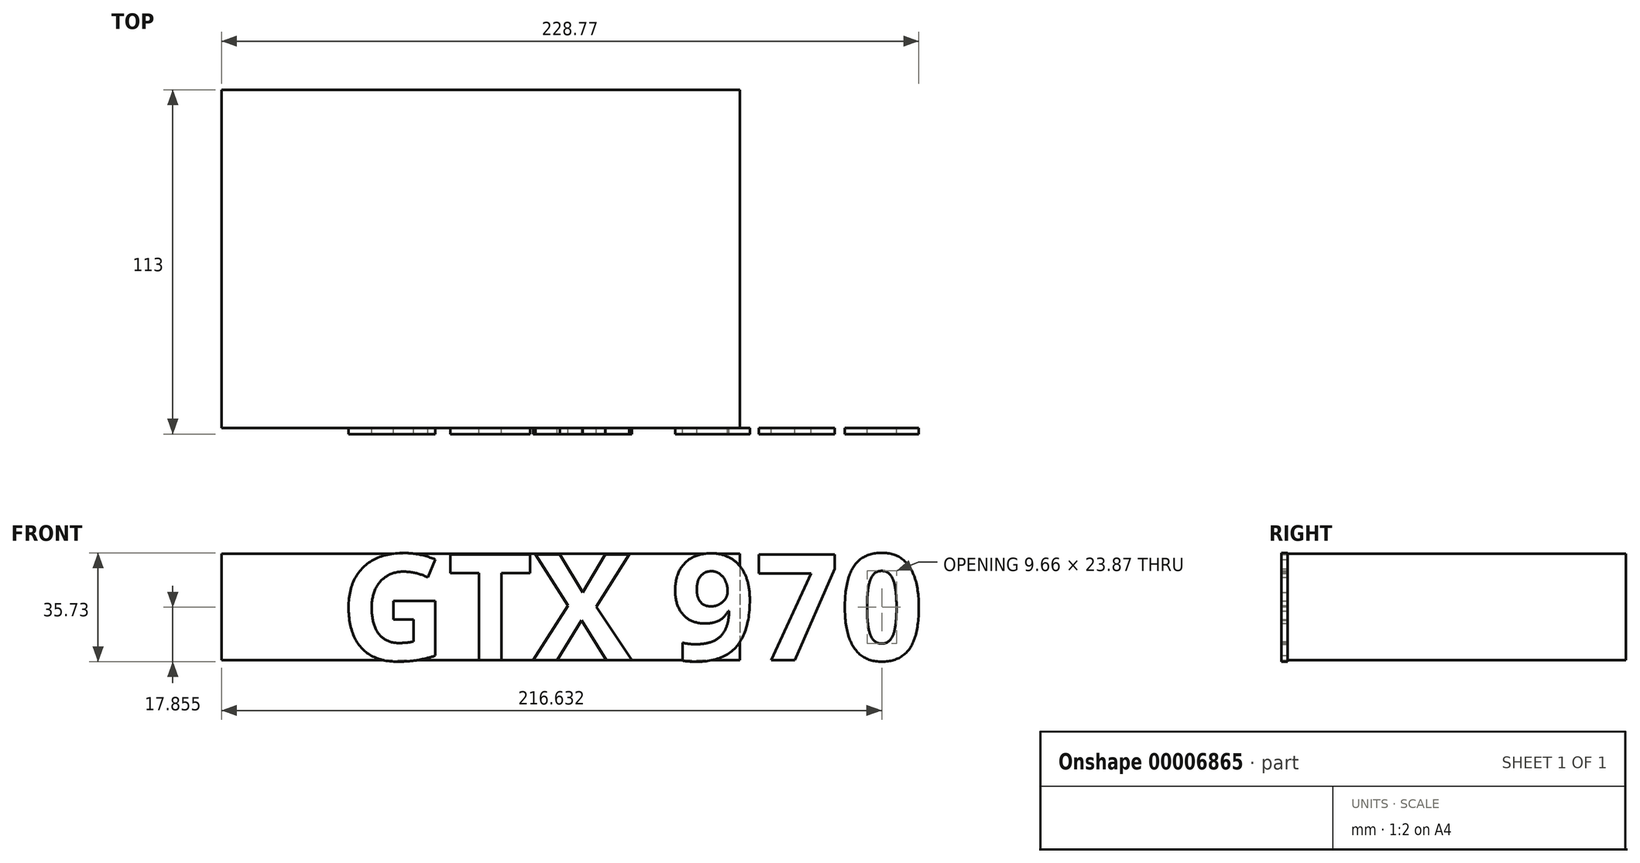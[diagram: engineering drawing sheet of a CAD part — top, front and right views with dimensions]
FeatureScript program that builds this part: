
annotation { "Feature Type Name" : "Feature", "Feature Type Description" : "" }
export const myFeature = defineFeature(function(context is Context, id is Id, definition is map)
    precondition{}
    {
        {
            var Q0;
            Q0=qCreatedBy(makeId("Top.planeOp"),FACE);
            var sketch = newSketch(context, id + "F0", { "sketchPlane" : qUnion([Q0])});
            skLineSegment(sketch, "E0.bottom", {"start": v(-100.66, 0) * mm, "end": v(69.34, 0) * mm});
            skLineSegment(sketch, "E0.top", {"start": v(-100.66, 111) * mm, "end": v(69.34, 111) * mm});
            skLineSegment(sketch, "E0.left", {"start": v(-100.66, 0) * mm, "end": v(-100.66, 111) * mm});
            skLineSegment(sketch, "E0.right", {"start": v(69.34, 0) * mm, "end": v(69.34, 111) * mm});
            skSolve(sketch);
        }
        {
            var Q0;
            Q0=qSketchRegion(id+"F0",true);
            extrude(context, id + "F1", {"entities" : qUnion([Q0]), "depth" : 35 * mm});
        }
        {
            var Q0;
            Q0=makeQuery(id+"F1.opExtrude","SWEPT_FACE",FACE,{"disambiguationData":[OSD([sQuery(id+"F0.wireOp",EDGE,"E0.bottom")])]});
            var sketch = newSketch(context, id + "F2", { "sketchPlane" : qUnion([Q0])});
            skText(sketch, "E1", { "text": "GTX 970", "fontName": "OpenSans-Bold.ttf"});
            const initialGuessF2  = {"E1": [-0.0618, 0, 1, 0, 0.035]};
            skSetInitialGuess(sketch, initialGuessF2);
            skSolve(sketch);
        }
        {
            var Q0;
            Q0=qSketchRegion(id+"F2",true);
            extrude(context, id + "F3", {"entities" : qUnion([Q0]), "operationType" : NewBodyOperationType.ADD, "depth" : 2 * mm});
        }
    });
